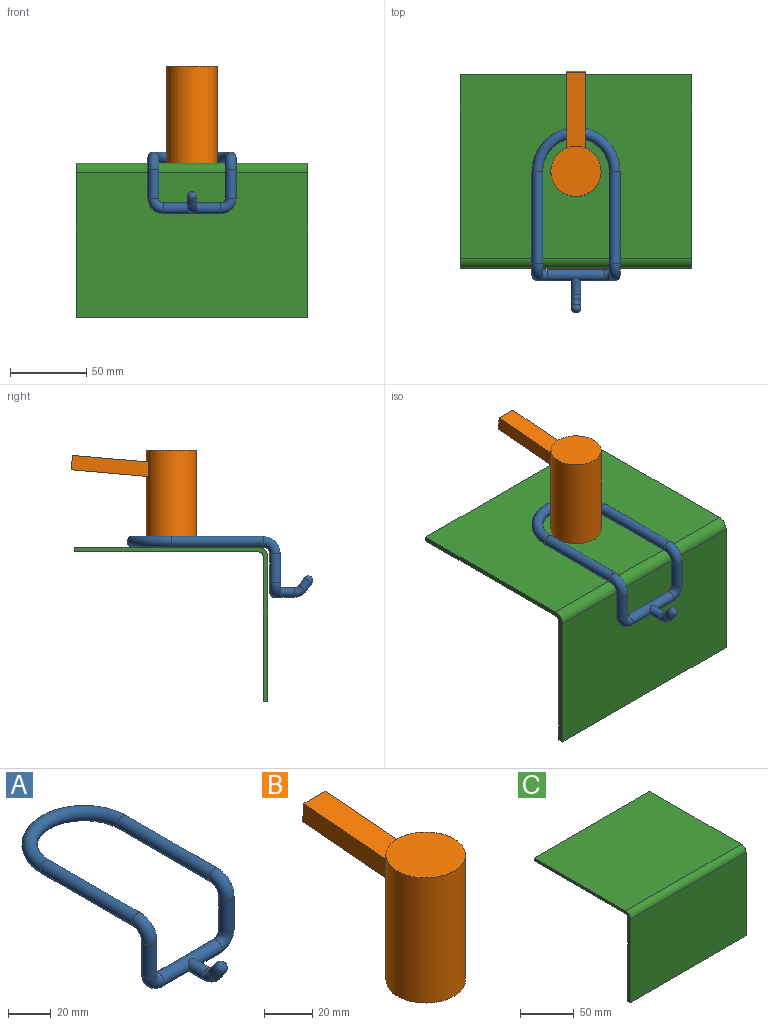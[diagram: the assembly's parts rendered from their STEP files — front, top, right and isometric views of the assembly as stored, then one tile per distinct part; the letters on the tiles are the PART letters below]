
ASSEMBLY  parts=3 mates=2
PART A: 14 faces, bbox 62.7x124.3x42.2 mm
  f0: torus R=25.4mm, axis (0,0,-1), area 1790.9mm2, adj f1,f6
  f1: cylinder r=3.57mm len=60.33mm, axis (0,-1,0), area 1353.9mm2, adj f0,f2
  f2: torus R=7.94mm, axis (1,0,0), area 279.8mm2, adj f1,f3
  f3: cylinder r=3.57mm len=19.05mm, axis (0,0,-1), area 427.5mm2, adj f2,f4
  f4: torus R=6.35mm, axis (0,1,0), area 223.9mm2, adj f3,f5
  f5: cylinder r=3.57mm len=38.1mm, axis (-1,0,0), area 818.6mm2, adj f4,f9,f10
  f6: cylinder r=3.57mm len=60.33mm, axis (0,-1,0), area 1353.9mm2, adj f0,f7
  f7: torus R=7.94mm, axis (-1,0,0), area 279.8mm2, adj f6,f8
  f8: cylinder r=3.57mm len=19.05mm, axis (0,0,-1), area 427.5mm2, adj f7,f9
  f9: torus R=6.35mm, axis (0,1,0), area 223.9mm2, adj f5,f8
  f10: cylinder r=3.17mm len=11.06mm, axis (0,-1,0), area 199.6mm2, adj f5,f11
  f11: torus R=6.35mm, axis (-1,0,0), area 121.6mm2, adj f10,f12
  f12: cylinder r=3.17mm len=8.84mm, axis (0,-0.57,0.82), area 126.7mm2, adj f11,f13
  f13: sphere r=3.17mm, area 63.3mm2, adj f12
PART B: 8 faces, bbox 33x82.4x63.5 mm
  f0: cylinder r=16.5mm len=63.5mm, axis (0,0,-1), area 6458.6mm2, adj f1,f2,f3,f4,f5,f6
  f1: plane 33x33mm, normal (0,0,1), area 855.3mm2, adj f0
  f2: plane 33x33mm, normal (0,0,-1), area 855.3mm2, adj f0
  f3: plane 50.69x13.92mm, normal (1,0,0), area 480.7mm2, adj f0,f5,f6,f7
  f4: plane 50.69x13.92mm, normal (-1,0,0), area 480.7mm2, adj f0,f5,f6,f7
  f5: plane 49.86x12.7mm, normal (0,-0.09,1), area 624.7mm2, adj f0,f3,f4,f7
  f6: plane 50.69x12.7mm, normal (0,0.09,-1), area 635.3mm2, adj f0,f3,f4,f7
  f7: plane 12.7x9.49mm, normal (0,1,0.09), area 121mm2, adj f3,f4,f5,f6
PART C: 10 faces, bbox 152.4x127x101.6 mm
  f0: plane 152.4x3.18mm, normal (0,1,0), area 483.9mm2, adj f1,f7,f8,f9
  f1: plane 152.4x120.65mm, normal (0,0,1), area 18387.1mm2, adj f0,f2,f8,f9
  f2: cylinder r=6.35mm len=152.4mm, axis (-1,0,0), area 1520.1mm2, adj f1,f3,f8,f9
  f3: plane 152.4x95.25mm, normal (0,-1,0), area 14516.1mm2, adj f2,f4,f8,f9
  f4: plane 152.4x3.18mm, normal (0,0,-1), area 483.9mm2, adj f3,f5,f8,f9
  f5: plane 152.4x95.25mm, normal (0,1,0), area 14516.1mm2, adj f4,f6,f8,f9
  f6: cylinder r=3.17mm len=152.4mm, axis (-1,0,0), area 760.1mm2, adj f5,f7,f8,f9
  f7: plane 152.4x120.65mm, normal (0,0,-1), area 18387.1mm2, adj f0,f6,f8,f9
  f8: plane 127x101.6mm, normal (1,0,0), area 709.2mm2, adj f0,f1,f2,f3,f4,f5,f6,f7
  f9: plane 127x101.6mm, normal (-1,0,0), area 709.2mm2, adj f0,f1,f2,f3,f4,f5,f6,f7
PLACE A t=(0,-31.75,3.57)mm
PLACE B t=(0,-31.75,0)mm
PLACE C t=(0,-95.25,0)mm fixed
MATE fastened C.f1 <-> B.f2  axis (0,0,1) through (0,-88.9,0)mm
MATE fastened A.f0 <-> B.f0  axis (0,0,-1) through (0,-31.75,3.57)mm
